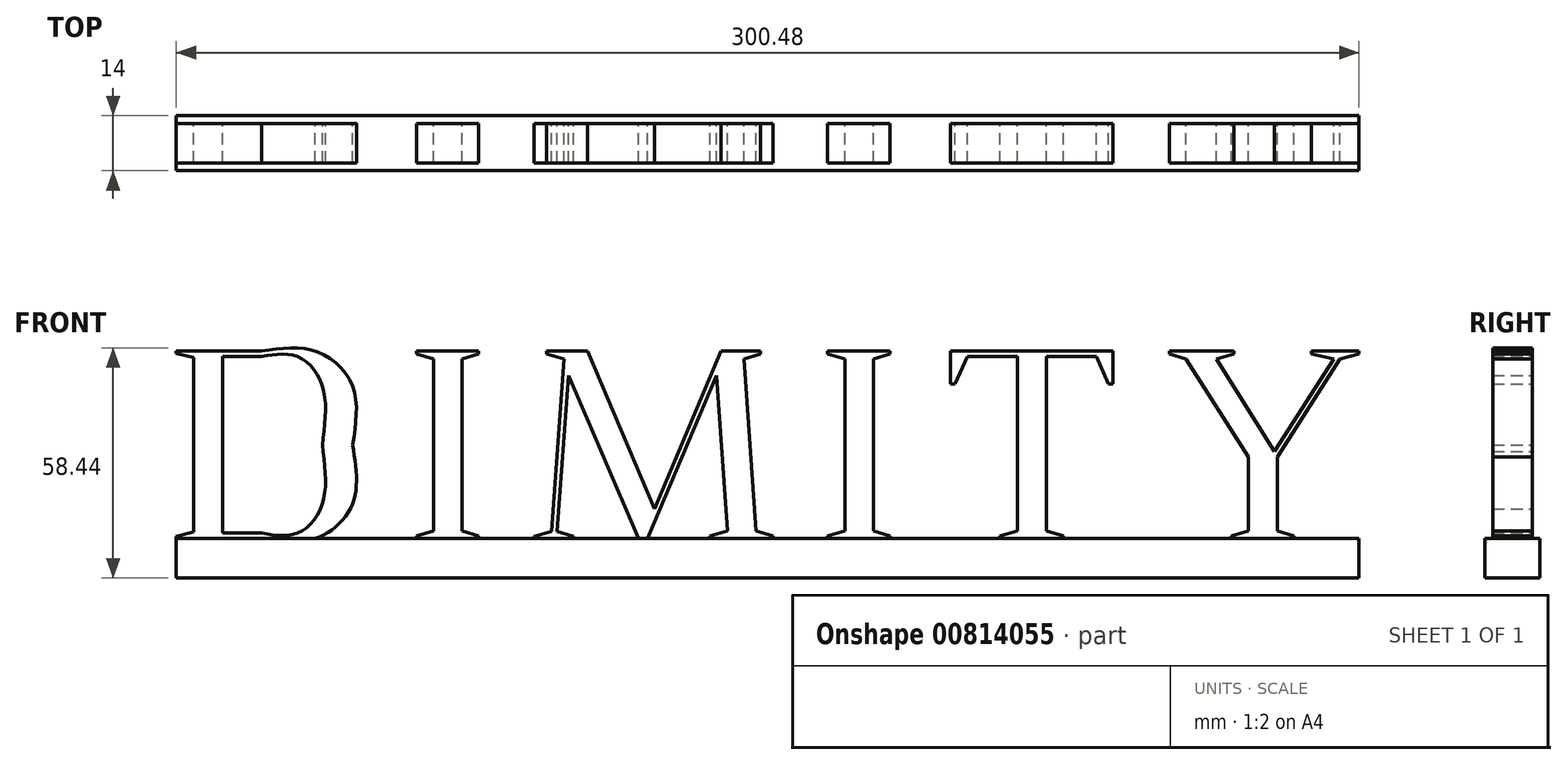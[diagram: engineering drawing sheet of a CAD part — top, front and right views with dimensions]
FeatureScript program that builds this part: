
annotation { "Feature Type Name" : "Feature", "Feature Type Description" : "" }
export const myFeature = defineFeature(function(context is Context, id is Id, definition is map)
    precondition{}
    {
        {
            var Q0;
            Q0=qCreatedBy(makeId("Front.planeOp"),FACE);
            var sketch = newSketch(context, id + "F0", { "sketchPlane" : qUnion([Q0])});
            skLineSegment(sketch, "E0", {"start": v(-150.24, 61.58) * mm, "end": v(-150.24, 60.97) * mm});
            skLineSegment(sketch, "E1", {"start": v(-150.24, 60.97) * mm, "end": v(-145.82, 59.95) * mm});
            skLineSegment(sketch, "E2", {"start": v(-145.82, 59.95) * mm, "end": v(-145.82, 15.6) * mm});
            skLineSegment(sketch, "E3", {"start": v(-145.82, 15.6) * mm, "end": v(-150.24, 14.5) * mm});
            skLineSegment(sketch, "E4", {"start": v(-150.24, 14.5) * mm, "end": v(-150.24, 13.96) * mm});
            skLineSegment(sketch, "E5", {"start": v(-150.24, 13.96) * mm, "end": v(-128.54, 13.96) * mm});
            skFitSpline(sketch, "E6", {"points": [v(-128.54, 13.96) * mm, v(-114.94, 13.96) * mm, v(-105.41, 22.8) * mm, v(-105.41, 37.77) * mm]});
            skFitSpline(sketch, "E7", {"points": [v(-105.41, 37.77) * mm, v(-105.41, 52.6) * mm, v(-114.94, 61.58) * mm, v(-128.54, 61.58) * mm]});
            skLineSegment(sketch, "E8", {"start": v(-128.54, 61.58) * mm, "end": v(-150.24, 61.58) * mm});
            skLineSegment(sketch, "E9", {"start": v(-138.48, 60.22) * mm, "end": v(-128.54, 60.22) * mm});
            skFitSpline(sketch, "E10", {"points": [v(-128.54, 60.22) * mm, v(-119.56, 60.22) * mm, v(-113.1, 52.74) * mm, v(-113.1, 37.7) * mm]});
            skFitSpline(sketch, "E11", {"points": [v(-113.1, 37.7) * mm, v(-113.1, 22.74) * mm, v(-119.56, 15.32) * mm, v(-128.54, 15.32) * mm]});
            skLineSegment(sketch, "E12", {"start": v(-128.54, 15.32) * mm, "end": v(-138.48, 15.32) * mm});
            skLineSegment(sketch, "E13", {"start": v(-138.48, 15.32) * mm, "end": v(-138.48, 60.22) * mm});
            skLineSegment(sketch, "E14", {"start": v(-89.22, 61.58) * mm, "end": v(-89.22, 60.9) * mm});
            skLineSegment(sketch, "E15", {"start": v(-89.22, 60.9) * mm, "end": v(-84.8, 59.6) * mm});
            skLineSegment(sketch, "E16", {"start": v(-84.8, 59.6) * mm, "end": v(-84.8, 15.93) * mm});
            skLineSegment(sketch, "E17", {"start": v(-84.8, 15.93) * mm, "end": v(-89.22, 14.64) * mm});
            skLineSegment(sketch, "E18", {"start": v(-89.22, 14.64) * mm, "end": v(-89.22, 13.96) * mm});
            skLineSegment(sketch, "E19", {"start": v(-89.22, 13.96) * mm, "end": v(-73.37, 13.96) * mm});
            skLineSegment(sketch, "E20", {"start": v(-73.37, 13.96) * mm, "end": v(-73.37, 14.64) * mm});
            skLineSegment(sketch, "E21", {"start": v(-73.37, 14.64) * mm, "end": v(-77.59, 15.93) * mm});
            skLineSegment(sketch, "E22", {"start": v(-77.59, 15.93) * mm, "end": v(-77.59, 59.6) * mm});
            skLineSegment(sketch, "E23", {"start": v(-77.59, 59.6) * mm, "end": v(-73.37, 60.9) * mm});
            skLineSegment(sketch, "E24", {"start": v(-73.37, 60.9) * mm, "end": v(-73.37, 61.58) * mm});
            skLineSegment(sketch, "E25", {"start": v(-73.37, 61.58) * mm, "end": v(-89.22, 61.58) * mm});
            skLineSegment(sketch, "E26", {"start": v(-56.1, 61.58) * mm, "end": v(-56.1, 60.9) * mm});
            skLineSegment(sketch, "E27", {"start": v(-56.1, 60.9) * mm, "end": v(-51.67, 59.6) * mm});
            skLineSegment(sketch, "E28", {"start": v(-51.67, 59.6) * mm, "end": v(-54.87, 15.8) * mm});
            skLineSegment(sketch, "E29", {"start": v(-54.87, 15.8) * mm, "end": v(-59.29, 14.5) * mm});
            skLineSegment(sketch, "E30", {"start": v(-59.29, 14.5) * mm, "end": v(-59.29, 13.96) * mm});
            skLineSegment(sketch, "E31", {"start": v(-59.29, 13.96) * mm, "end": v(-49.29, 13.96) * mm});
            skLineSegment(sketch, "E32", {"start": v(-49.29, 13.96) * mm, "end": v(-49.29, 14.5) * mm});
            skLineSegment(sketch, "E33", {"start": v(-49.29, 14.5) * mm, "end": v(-53.44, 15.8) * mm});
            skLineSegment(sketch, "E34", {"start": v(-53.44, 15.8) * mm, "end": v(-50.51, 55.4) * mm});
            skLineSegment(sketch, "E35", {"start": v(-50.51, 55.4) * mm, "end": v(-32.76, 13.96) * mm});
            skLineSegment(sketch, "E36", {"start": v(-32.76, 13.96) * mm, "end": v(-30.51, 13.96) * mm});
            skLineSegment(sketch, "E37", {"start": v(-30.51, 13.96) * mm, "end": v(-13.03, 55.32) * mm});
            skLineSegment(sketch, "E38", {"start": v(-13.03, 55.32) * mm, "end": v(-10.17, 15.93) * mm});
            skLineSegment(sketch, "E39", {"start": v(-10.17, 15.93) * mm, "end": v(-14.6, 14.64) * mm});
            skLineSegment(sketch, "E40", {"start": v(-14.6, 14.64) * mm, "end": v(-14.6, 13.96) * mm});
            skLineSegment(sketch, "E41", {"start": v(-14.6, 13.96) * mm, "end": v(1.32, 13.96) * mm});
            skLineSegment(sketch, "E42", {"start": v(1.32, 13.96) * mm, "end": v(1.32, 14.64) * mm});
            skLineSegment(sketch, "E43", {"start": v(1.32, 14.64) * mm, "end": v(-2.9, 15.93) * mm});
            skLineSegment(sketch, "E44", {"start": v(-2.9, 15.93) * mm, "end": v(-6.02, 59.6) * mm});
            skLineSegment(sketch, "E45", {"start": v(-6.02, 59.6) * mm, "end": v(-1.8, 60.9) * mm});
            skLineSegment(sketch, "E46", {"start": v(-1.8, 60.9) * mm, "end": v(-1.8, 61.58) * mm});
            skLineSegment(sketch, "E47", {"start": v(-1.8, 61.58) * mm, "end": v(-11.8, 61.58) * mm});
            skLineSegment(sketch, "E48", {"start": v(-11.8, 61.58) * mm, "end": v(-28.68, 21.44) * mm});
            skLineSegment(sketch, "E49", {"start": v(-28.68, 21.44) * mm, "end": v(-45.68, 61.58) * mm});
            skLineSegment(sketch, "E50", {"start": v(-45.68, 61.58) * mm, "end": v(-56.1, 61.58) * mm});
            skLineSegment(sketch, "E51", {"start": v(15.27, 61.58) * mm, "end": v(15.27, 60.9) * mm});
            skLineSegment(sketch, "E52", {"start": v(15.27, 60.9) * mm, "end": v(19.7, 59.6) * mm});
            skLineSegment(sketch, "E53", {"start": v(19.7, 59.6) * mm, "end": v(19.7, 15.93) * mm});
            skLineSegment(sketch, "E54", {"start": v(19.7, 15.93) * mm, "end": v(15.27, 14.64) * mm});
            skLineSegment(sketch, "E55", {"start": v(15.27, 14.64) * mm, "end": v(15.27, 13.96) * mm});
            skLineSegment(sketch, "E56", {"start": v(15.27, 13.96) * mm, "end": v(31.12, 13.96) * mm});
            skLineSegment(sketch, "E57", {"start": v(31.12, 13.96) * mm, "end": v(31.12, 14.64) * mm});
            skLineSegment(sketch, "E58", {"start": v(31.12, 14.64) * mm, "end": v(26.9, 15.93) * mm});
            skLineSegment(sketch, "E59", {"start": v(26.9, 15.93) * mm, "end": v(26.9, 59.6) * mm});
            skLineSegment(sketch, "E60", {"start": v(26.9, 59.6) * mm, "end": v(31.12, 60.9) * mm});
            skLineSegment(sketch, "E61", {"start": v(31.12, 60.9) * mm, "end": v(31.12, 61.58) * mm});
            skLineSegment(sketch, "E62", {"start": v(31.12, 61.58) * mm, "end": v(15.27, 61.58) * mm});
            skLineSegment(sketch, "E63", {"start": v(46.5, 61.58) * mm, "end": v(46.5, 53.21) * mm});
            skLineSegment(sketch, "E64", {"start": v(46.5, 53.21) * mm, "end": v(47.59, 53.21) * mm});
            skLineSegment(sketch, "E65", {"start": v(47.59, 53.21) * mm, "end": v(50.79, 60.22) * mm});
            skLineSegment(sketch, "E66", {"start": v(50.79, 60.22) * mm, "end": v(63.44, 60.22) * mm});
            skLineSegment(sketch, "E67", {"start": v(63.44, 60.22) * mm, "end": v(63.44, 15.93) * mm});
            skLineSegment(sketch, "E68", {"start": v(63.44, 15.93) * mm, "end": v(59.02, 14.64) * mm});
            skLineSegment(sketch, "E69", {"start": v(59.02, 14.64) * mm, "end": v(59.02, 13.96) * mm});
            skLineSegment(sketch, "E70", {"start": v(59.02, 13.96) * mm, "end": v(75.2, 13.96) * mm});
            skLineSegment(sketch, "E71", {"start": v(75.2, 13.96) * mm, "end": v(75.2, 14.64) * mm});
            skLineSegment(sketch, "E72", {"start": v(75.2, 14.64) * mm, "end": v(70.79, 15.93) * mm});
            skLineSegment(sketch, "E73", {"start": v(70.79, 15.93) * mm, "end": v(70.79, 60.22) * mm});
            skLineSegment(sketch, "E74", {"start": v(70.79, 60.22) * mm, "end": v(83.5, 60.22) * mm});
            skLineSegment(sketch, "E75", {"start": v(83.5, 60.22) * mm, "end": v(86.64, 53.21) * mm});
            skLineSegment(sketch, "E76", {"start": v(86.64, 53.21) * mm, "end": v(87.8, 53.21) * mm});
            skLineSegment(sketch, "E77", {"start": v(87.8, 53.21) * mm, "end": v(87.8, 61.58) * mm});
            skLineSegment(sketch, "E78", {"start": v(87.8, 61.58) * mm, "end": v(46.5, 61.58) * mm});
            skLineSegment(sketch, "E79", {"start": v(102.08, 61.58) * mm, "end": v(102.08, 60.9) * mm});
            skLineSegment(sketch, "E80", {"start": v(102.08, 60.9) * mm, "end": v(106.3, 59.6) * mm});
            skLineSegment(sketch, "E81", {"start": v(106.3, 59.6) * mm, "end": v(122.22, 34.64) * mm});
            skLineSegment(sketch, "E82", {"start": v(122.22, 34.64) * mm, "end": v(122.22, 15.93) * mm});
            skLineSegment(sketch, "E83", {"start": v(122.22, 15.93) * mm, "end": v(117.8, 14.64) * mm});
            skLineSegment(sketch, "E84", {"start": v(117.8, 14.64) * mm, "end": v(117.8, 13.96) * mm});
            skLineSegment(sketch, "E85", {"start": v(117.8, 13.96) * mm, "end": v(133.71, 13.96) * mm});
            skLineSegment(sketch, "E86", {"start": v(133.71, 13.96) * mm, "end": v(133.71, 14.64) * mm});
            skLineSegment(sketch, "E87", {"start": v(133.71, 14.64) * mm, "end": v(129.5, 15.93) * mm});
            skLineSegment(sketch, "E88", {"start": v(129.5, 15.93) * mm, "end": v(129.5, 34.64) * mm});
            skLineSegment(sketch, "E89", {"start": v(129.5, 34.64) * mm, "end": v(145.41, 59.6) * mm});
            skLineSegment(sketch, "E90", {"start": v(145.41, 59.6) * mm, "end": v(150.24, 60.9) * mm});
            skLineSegment(sketch, "E91", {"start": v(150.24, 60.9) * mm, "end": v(150.24, 61.58) * mm});
            skLineSegment(sketch, "E92", {"start": v(150.24, 61.58) * mm, "end": v(138.14, 61.58) * mm});
            skLineSegment(sketch, "E93", {"start": v(138.14, 61.58) * mm, "end": v(138.14, 60.9) * mm});
            skLineSegment(sketch, "E94", {"start": v(138.14, 60.9) * mm, "end": v(143.85, 59.6) * mm});
            skLineSegment(sketch, "E95", {"start": v(143.85, 59.6) * mm, "end": v(128.82, 36.14) * mm});
            skLineSegment(sketch, "E96", {"start": v(128.82, 36.14) * mm, "end": v(113.99, 59.6) * mm});
            skLineSegment(sketch, "E97", {"start": v(113.99, 59.6) * mm, "end": v(118.48, 60.9) * mm});
            skLineSegment(sketch, "E98", {"start": v(118.48, 60.9) * mm, "end": v(118.48, 61.58) * mm});
            skLineSegment(sketch, "E99", {"start": v(118.48, 61.58) * mm, "end": v(102.08, 61.58) * mm});
            skSolve(sketch);
        }
        {
            var Q0;
            Q0=qSketchRegion(id+"F0",true);
            extrude(context, id + "F1", {"entities" : qUnion([Q0]), "depth" : 10 * mm, "offsetDistance" : 25 * mm});
        }
        {
            var Q0;
            Q0=qCreatedBy(makeId("Front.planeOp"),FACE);
            var sketch = newSketch(context, id + "F2", { "sketchPlane" : qUnion([Q0])});
            skLineSegment(sketch, "E100.bottom", {"start": v(-150.24, 13.96) * mm, "end": v(150.24, 13.96) * mm});
            skLineSegment(sketch, "E100.top", {"start": v(-150.24, 3.96) * mm, "end": v(150.24, 3.96) * mm});
            skLineSegment(sketch, "E100.left", {"start": v(-150.24, 13.96) * mm, "end": v(-150.24, 3.96) * mm});
            skLineSegment(sketch, "E100.right", {"start": v(150.24, 13.96) * mm, "end": v(150.24, 3.96) * mm});
            skLineSegment(sketch, "E101", {"start": v(150.24, 61.6) * mm, "end": v(150.24, 2.87) * mm, "construction": true});
            skSolve(sketch);
        }
        {
            var Q0;
            Q0=makeQuery(id+"F2.imprint","IMPRINT",FACE,{"disambiguationData":[TD([[makeQuery(id+"F2.imprint","IMPRINT",EDGE,{"derivedFrom":sQuery(id+"F2.wireOp",EDGE,"E100.bottom")}),-1.0]])]});
            extrude(context, id + "F3", {"entities" : qUnion([Q0]), "operationType" : NewBodyOperationType.ADD, "depth" : 12 * mm, "offsetDistance" : 25 * mm, "hasSecondDirection" : true, "secondDirectionOppositeDirection" : true, "secondDirectionDepth" : 2 * mm});
        }
    });
